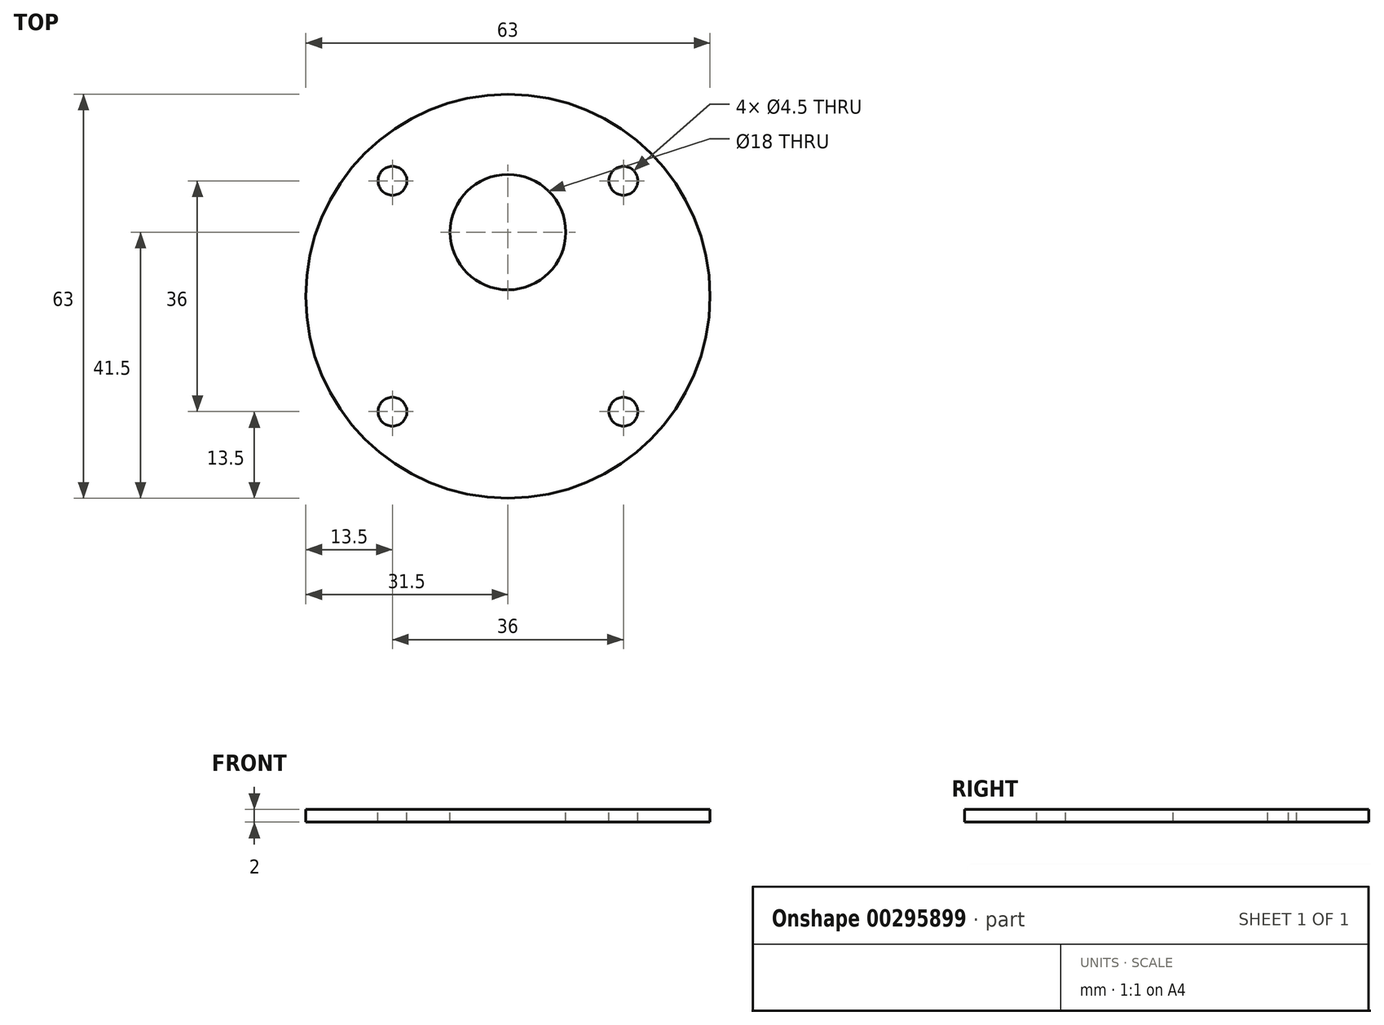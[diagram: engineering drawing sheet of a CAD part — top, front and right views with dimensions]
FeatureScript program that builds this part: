
annotation { "Feature Type Name" : "Feature", "Feature Type Description" : "" }
export const myFeature = defineFeature(function(context is Context, id is Id, definition is map)
    precondition{}
    {
        {
            var Q0;
            Q0=qCreatedBy(makeId("Top.planeOp"),FACE);
            var sketch = newSketch(context, id + "F0", { "sketchPlane" : qUnion([Q0])});
            skCircle(sketch, "E0", {"center": v(0, 3) * mm, "radius": 11.5 * mm});
            skCircle(sketch, "E1", {"center": v(0, 3) * mm, "radius": 6 * mm});
            skLineSegment(sketch, "E2.bottom", {"start": v(-18, -25) * mm, "end": v(18, -25) * mm, "construction": true});
            skLineSegment(sketch, "E2.top", {"start": v(-18, 11) * mm, "end": v(18, 11) * mm, "construction": true});
            skLineSegment(sketch, "E2.left", {"start": v(-18, -25) * mm, "end": v(-18, 11) * mm, "construction": true});
            skLineSegment(sketch, "E2.right", {"start": v(18, -25) * mm, "end": v(18, 11) * mm, "construction": true});
            skLineSegment(sketch, "E3", {"start": v(18, 11) * mm, "end": v(-18, -25) * mm, "construction": true});
            skLineSegment(sketch, "E4", {"start": v(-18, 11) * mm, "end": v(18, -25) * mm, "construction": true});
            skCircle(sketch, "E5", {"center": v(0, -7) * mm, "radius": 31.5 * mm});
            skCircle(sketch, "E6", {"center": v(-18, 11) * mm, "radius": 2.25 * mm});
            skCircle(sketch, "E7.MirrorC", {"center": v(18, 11) * mm, "radius": 2.25 * mm});
            skCircle(sketch, "E8", {"center": v(-18, -25) * mm, "radius": 2.25 * mm});
            skCircle(sketch, "E9", {"center": v(18, -25) * mm, "radius": 2.25 * mm});
            skCircle(sketch, "E10", {"center": v(0, 3) * mm, "radius": 9 * mm});
            skLineSegment(sketch, "E11", {"start": v(0, -7) * mm, "end": v(0, 3) * mm, "construction": true});
            skSolve(sketch);
        }
        {
            var Q0;
            Q0=makeQuery(id+"F0.imprint","IMPRINT",FACE,{"disambiguationData":[TD([[makeQuery(id+"F0.imprint","IMPRINT",EDGE,{"derivedFrom":sQuery(id+"F0.wireOp",EDGE,"E5")}),1.0]])]});
            var Q1;
            Q1=makeQuery(id+"F0.imprint","IMPRINT",FACE,{"disambiguationData":[TD([[makeQuery(id+"F0.imprint","IMPRINT",EDGE,{"derivedFrom":sQuery(id+"F0.wireOp",EDGE,"E0")}),1.0]])]});
            extrude(context, id + "F1", {"entities" : qUnion([Q0, Q1]), "oppositeDirection" : true, "depth" : 2 * mm});
        }
    });
